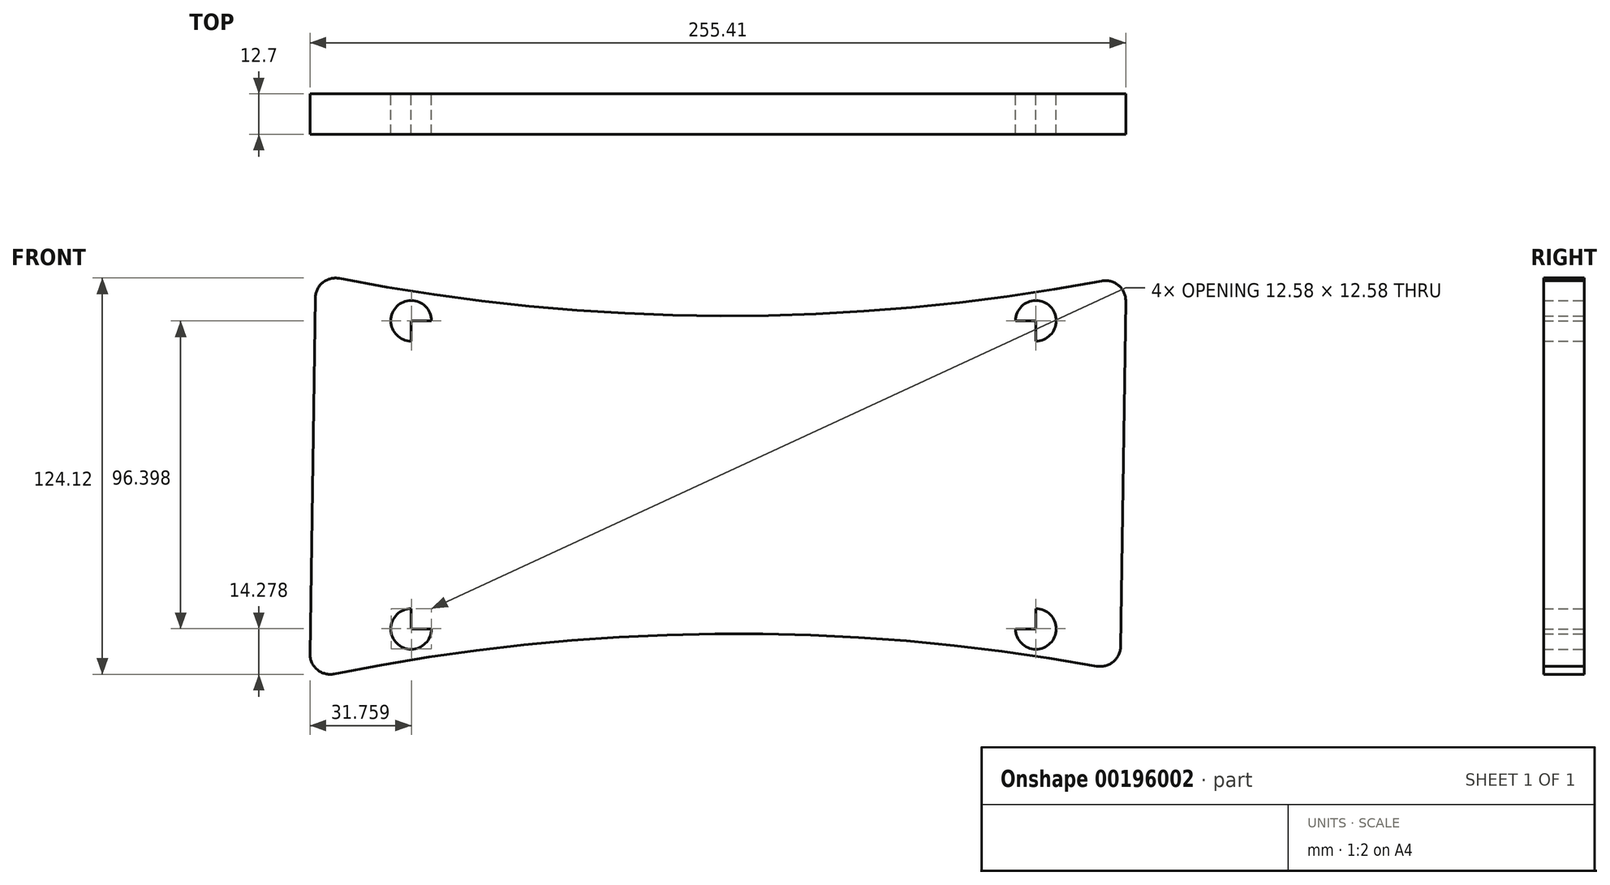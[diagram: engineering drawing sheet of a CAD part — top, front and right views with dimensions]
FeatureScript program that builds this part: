
annotation { "Feature Type Name" : "Feature", "Feature Type Description" : "" }
export const myFeature = defineFeature(function(context is Context, id is Id, definition is map)
    precondition{}
    {
        {
            var Q0;
            Q0=qCreatedBy(makeId("Front.planeOp"),FACE);
            var sketch = newSketch(context, id + "F0", { "sketchPlane" : qUnion([Q0])});
            skLineSegment(sketch, "E0.left", {"start": v(-119.35, 53.95) * mm, "end": v(-121.02, -57.47) * mm});
            skLineSegment(sketch, "E0.right", {"start": v(134.4, 52.95) * mm, "end": v(132.77, -55.19) * mm});
            skArc(sketch, "E1", {"start": v(-111.79, 60.1) * mm, "mid": v(7.5, 48.38) * mm, "end": v(126.87, 59.29) * mm});
            skArc(sketch, "E2.MirrorCS", {"start": v(-113.42, -63.79) * mm, "mid": v(5.82, -51.25) * mm, "end": v(125.29, -61.34) * mm});
            skPoint(sketch, "E3.visualSharp", {"position": v(-119.23, 61.59) * mm});
            skArc(sketch, "E3.filletArc", {"start": v(-111.79, 60.1) * mm, "mid": v(-117, 58.79) * mm, "end": v(-119.35, 53.95) * mm});
            skPoint(sketch, "E4.visualSharp", {"position": v(134.5, 60.77) * mm});
            skArc(sketch, "E4.filletArc", {"start": v(134.4, 52.95) * mm, "mid": v(132.13, 57.9) * mm, "end": v(126.87, 59.29) * mm});
            skPoint(sketch, "E5.visualSharp", {"position": v(132.65, -62.72) * mm});
            skArc(sketch, "E5.filletArc", {"start": v(125.29, -61.34) * mm, "mid": v(130.45, -60) * mm, "end": v(132.77, -55.19) * mm});
            skPoint(sketch, "E6.visualSharp", {"position": v(-121.14, -65.4) * mm});
            skArc(sketch, "E6.filletArc", {"start": v(-121.02, -57.47) * mm, "mid": v(-118.73, -62.45) * mm, "end": v(-113.42, -63.79) * mm});
            skCircle(sketch, "E7", {"center": v(-89.32, 46.83) * mm, "radius": 6.35 * mm});
            skCircle(sketch, "E8", {"center": v(-89.32, -49.7) * mm, "radius": 6.35 * mm});
            skCircle(sketch, "E9", {"center": v(106.26, 46.83) * mm, "radius": 6.35 * mm});
            skCircle(sketch, "E10", {"center": v(106.26, -49.7) * mm, "radius": 6.35 * mm});
            skLineSegment(sketch, "E11", {"start": v(-89.32, 46.83) * mm, "end": v(-89.32, -49.7) * mm});
            skLineSegment(sketch, "E12", {"start": v(-89.32, -49.7) * mm, "end": v(106.26, -49.7) * mm});
            skLineSegment(sketch, "E13", {"start": v(106.26, -49.7) * mm, "end": v(106.26, 46.83) * mm});
            skLineSegment(sketch, "E14", {"start": v(106.26, 46.83) * mm, "end": v(-89.32, 46.83) * mm});
            skSolve(sketch);
        }
        {
            var Q0;
            Q0=makeQuery(id+"F0.imprint","IMPRINT",FACE,{"disambiguationData":[TD([[makeQuery(id+"F0.imprint","IMPRINT",EDGE,{"derivedFrom":sQuery(id+"F0.wireOp",EDGE,"E0.left")}),1.0]])]});
            var Q1;
            {var subQ9=sQuery(id+"F0.wireOp",EDGE,"E11");var subQ13=sQuery(id+"F0.wireOp",EDGE,"E7");var subQ14=makeQuery(id+"F0.imprint","INTERSECT",VERTEX,{"derivedFrom":[subQ13,subQ9]});Q1=makeQuery(id+"F0.imprint","IMPRINT",FACE,{"disambiguationData":[TD([[makeQuery(id+"F0.imprint","IMPRINT",EDGE,{"disambiguationData":[TD([[subQ14,-1.0]])],"derivedFrom":subQ13}),-1.0]])]});}
            var Q2;
            {var subQ0=sQuery(id+"F0.wireOp",EDGE,"E11");var subQ1=sQuery(id+"F0.wireOp",EDGE,"E7");var subQ2=makeQuery(id+"F0.imprint","INTERSECT",VERTEX,{"derivedFrom":[subQ1,subQ0]});Q2=makeQuery(id+"F0.imprint","IMPRINT",FACE,{"disambiguationData":[TD([[makeQuery(id+"F0.imprint","IMPRINT",EDGE,{"disambiguationData":[TD([[subQ2,-1.0]])],"derivedFrom":subQ1}),1.0]])]});}
            var Q3;
            {var subQ0=sQuery(id+"F0.wireOp",EDGE,"E11");var subQ1=sQuery(id+"F0.wireOp",EDGE,"E8");var subQ2=makeQuery(id+"F0.imprint","INTERSECT",VERTEX,{"derivedFrom":[subQ1,subQ0]});Q3=makeQuery(id+"F0.imprint","IMPRINT",FACE,{"disambiguationData":[TD([[makeQuery(id+"F0.imprint","IMPRINT",EDGE,{"disambiguationData":[TD([[subQ2,1.0]])],"derivedFrom":subQ1}),1.0]])]});}
            var Q4;
            {var subQ0=sQuery(id+"F0.wireOp",EDGE,"E13");var subQ1=sQuery(id+"F0.wireOp",EDGE,"E9");var subQ2=makeQuery(id+"F0.imprint","INTERSECT",VERTEX,{"derivedFrom":[subQ1,subQ0]});Q4=makeQuery(id+"F0.imprint","IMPRINT",FACE,{"disambiguationData":[TD([[makeQuery(id+"F0.imprint","IMPRINT",EDGE,{"disambiguationData":[TD([[subQ2,1.0]])],"derivedFrom":subQ1}),1.0]])]});}
            var Q5;
            {var subQ0=sQuery(id+"F0.wireOp",EDGE,"E12");var subQ1=sQuery(id+"F0.wireOp",EDGE,"E10");var subQ2=makeQuery(id+"F0.imprint","INTERSECT",VERTEX,{"derivedFrom":[subQ1,subQ0]});Q5=makeQuery(id+"F0.imprint","IMPRINT",FACE,{"disambiguationData":[TD([[makeQuery(id+"F0.imprint","IMPRINT",EDGE,{"disambiguationData":[TD([[subQ2,1.0]])],"derivedFrom":subQ1}),1.0]])]});}
            extrude(context, id + "F1", {"entities" : qUnion([Q0, Q1, Q2, Q3, Q4, Q5]), "depth" : 12.7 * mm});
        }
    });
